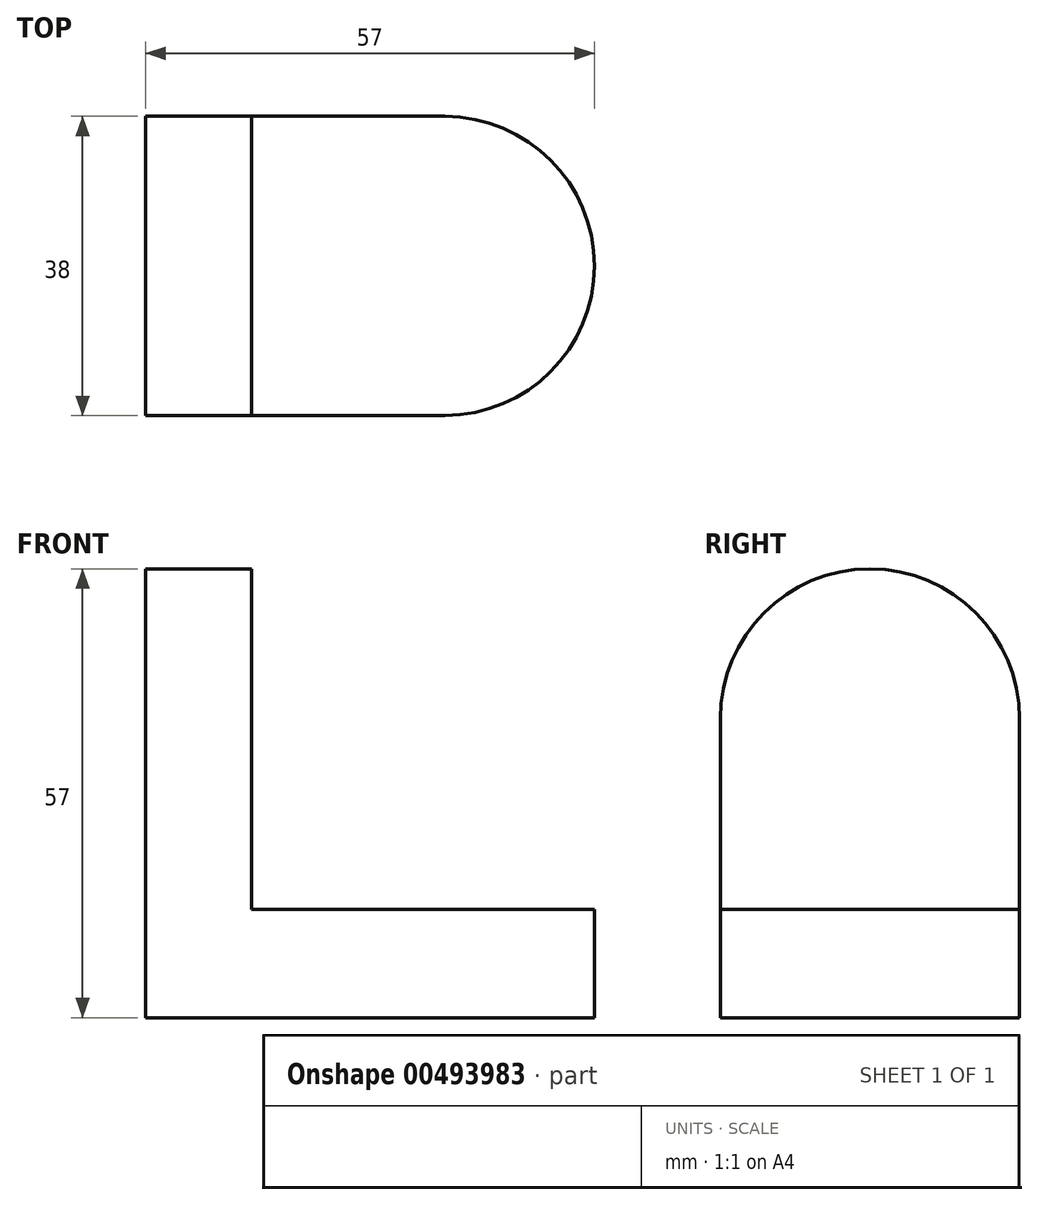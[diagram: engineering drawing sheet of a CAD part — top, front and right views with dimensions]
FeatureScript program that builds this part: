
annotation { "Feature Type Name" : "Feature", "Feature Type Description" : "" }
export const myFeature = defineFeature(function(context is Context, id is Id, definition is map)
    precondition{}
    {
        {
            var Q0;
            Q0=qCreatedBy(makeId("Front.planeOp"),FACE);
            var sketch = newSketch(context, id + "F0", { "sketchPlane" : qUnion([Q0])});
            skLineSegment(sketch, "E0.bottom", {"start": v(-33.44, 57) * mm, "end": v(-19.96, 57) * mm});
            skLineSegment(sketch, "E0.top", {"start": v(-33.44, 0) * mm, "end": v(-19.96, 0) * mm});
            skLineSegment(sketch, "E0.left", {"start": v(-33.44, 57) * mm, "end": v(-33.44, 0) * mm});
            skLineSegment(sketch, "E0.right", {"start": v(-19.96, 57) * mm, "end": v(-19.96, 13.76) * mm});
            skLineSegment(sketch, "E1.bottom", {"start": v(-33.44, 0) * mm, "end": v(23.56, 0) * mm});
            skLineSegment(sketch, "E1.top", {"start": v(-19.96, 13.76) * mm, "end": v(23.56, 13.76) * mm});
            skLineSegment(sketch, "E1.left", {"start": v(-33.44, 0) * mm, "end": v(-33.44, 13.76) * mm});
            skLineSegment(sketch, "E1.right", {"start": v(23.56, 0) * mm, "end": v(23.56, 13.76) * mm});
            skSolve(sketch);
        }
        {
            var Q0;
            Q0=makeQuery(id+"F0.imprint","IMPRINT",FACE,{"disambiguationData":[TD([[makeQuery(id+"F0.imprint","IMPRINT",EDGE,{"derivedFrom":sQuery(id+"F0.wireOp",EDGE,"E0.bottom")}),-1.0]])]});
            extrude(context, id + "F1", {"entities" : qUnion([Q0]), "depth" : 38 * mm});
        }
        {
            var Q0;
            Q0=makeQuery(id+"F1.opExtrude","CAP_EDGE",EDGE,{"disambiguationData":[OSD([sQuery(id+"F0.wireOp",EDGE,"E0.bottom")])],"isStart":false});
            var Q1;
            Q1=makeQuery(id+"F1.opExtrude","CAP_EDGE",EDGE,{"disambiguationData":[OSD([sQuery(id+"F0.wireOp",EDGE,"E0.bottom")])],"isStart":true});
            var Q2;
            Q2=makeQuery(id+"F1.opExtrude","CAP_EDGE",EDGE,{"disambiguationData":[OSD([sQuery(id+"F0.wireOp",EDGE,"E1.right")])],"isStart":true});
            var Q3;
            Q3=makeQuery(id+"F1.opExtrude","CAP_EDGE",EDGE,{"disambiguationData":[OSD([sQuery(id+"F0.wireOp",EDGE,"E1.right")])],"isStart":false});
            fillet(context, id + "F2", {"entities" : qUnion([Q0, Q1, Q2, Q3]), "radius" : 19 * mm, "tangentPropagation" : true, "allowEdgeOverflow" : false});
        }
    });
